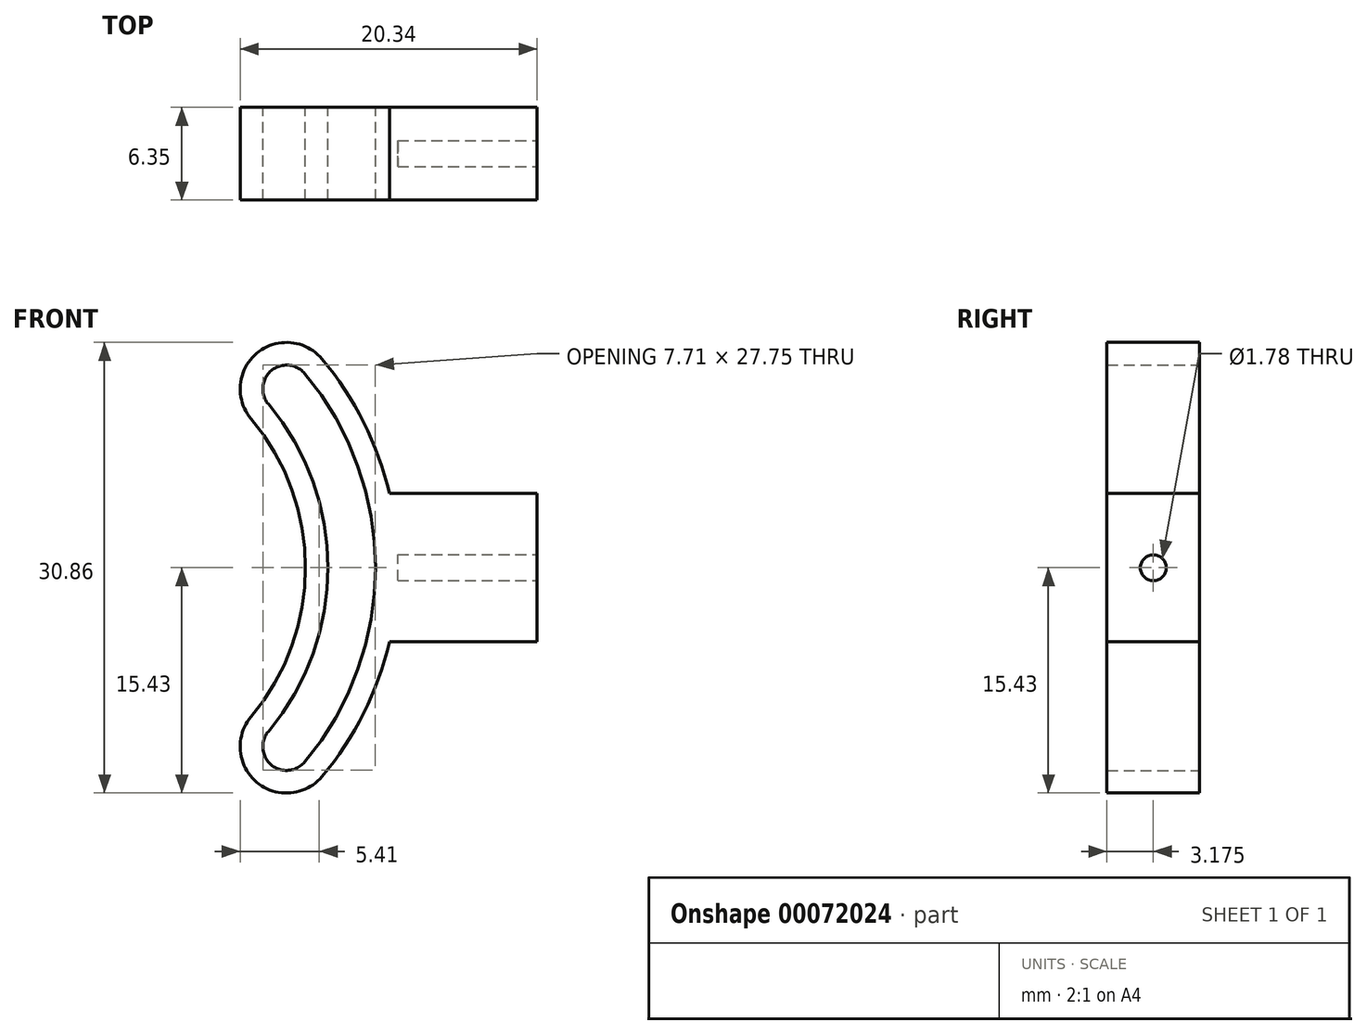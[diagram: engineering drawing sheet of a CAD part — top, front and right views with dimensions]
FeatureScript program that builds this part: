
annotation { "Feature Type Name" : "Feature", "Feature Type Description" : "" }
export const myFeature = defineFeature(function(context is Context, id is Id, definition is map)
    precondition{}
    {
        {
            var Q0;
            Q0=qCreatedBy(makeId("Front.planeOp"),FACE);
            var sketch = newSketch(context, id + "F0", { "sketchPlane" : qUnion([Q0])});
            skLineSegment(sketch, "E0.rect.bottom", {"start": v(5.08, 5.08) * mm, "end": v(-5.08, 5.08) * mm});
            skLineSegment(sketch, "E0.rect.top", {"start": v(5.08, -5.08) * mm, "end": v(-5.08, -5.08) * mm});
            skLineSegment(sketch, "E0.rect.left", {"start": v(5.08, 5.08) * mm, "end": v(5.08, -5.08) * mm});
            skLineSegment(sketch, "E0.rect.right", {"start": v(-5.08, 5.08) * mm, "end": v(-5.08, -5.08) * mm});
            skPoint(sketch, "E0.rect.middle", {"position": v(0, 0) * mm});
            skSolve(sketch);
        }
        {
            var Q0;
            Q0 = qSketchRegion(id + "F0", true);
            extrude(context, id + "F1", {"entities" : qUnion([Q0]), "depth" : 6.35 * mm});
        }
        {
            var Q0;
            Q0=makeQuery(id+"F1.opExtrude","SWEPT_FACE",FACE,{"disambiguationData":[OSD([sQuery(id+"F0.wireOp",EDGE,"E0.rect.left")])]});
            var sketch = newSketch(context, id + "F2", { "sketchPlane" : qUnion([Q0])});
            skCircle(sketch, "E1", {"center": v(-3.18, 0) * mm, "radius": 0.89 * mm});
            skPoint(sketch, "E1.centerSnap0", {"position": v(-6.35, 0) * mm});
            skSolve(sketch);
        }
        {
            var Q0;
            Q0 = qSketchRegion(id + "F2", true);
            extrude(context, id + "F3", {"entities" : qUnion([Q0]), "operationType" : NewBodyOperationType.REMOVE, "oppositeDirection" : true, "depth" : 25.4 * mm});
        }
        {
            var Q0;
            Q0=qCreatedBy(makeId("Front.planeOp"),FACE);
            var sketch = newSketch(context, id + "F4", { "sketchPlane" : qUnion([Q0])});
            skArc(sketch, "E2", {"start": v(-9.65, -14.3) * mm, "mid": v(-4.45, 0) * mm, "end": v(-9.65, 14.3) * mm});
            skArc(sketch, "E3", {"start": v(-9.65, 14.3) * mm, "mid": v(-14.13, 14.69) * mm, "end": v(-14.52, 10.21) * mm});
            skArc(sketch, "E4", {"start": v(-14.52, -10.21) * mm, "mid": v(-10.8, 0) * mm, "end": v(-14.52, 10.21) * mm});
            skArc(sketch, "E5", {"start": v(-14.52, -10.21) * mm, "mid": v(-14.13, -14.69) * mm, "end": v(-9.65, -14.3) * mm});
            skArc(sketch, "E6", {"start": v(-10.84, -13.3) * mm, "mid": v(-6, 0) * mm, "end": v(-10.84, 13.3) * mm});
            skArc(sketch, "E7", {"start": v(-10.84, 13.3) * mm, "mid": v(-13.13, 13.5) * mm, "end": v(-13.33, 11.2) * mm});
            skArc(sketch, "E8", {"start": v(-13.33, -11.2) * mm, "mid": v(-9.25, 0) * mm, "end": v(-13.33, 11.2) * mm});
            skArc(sketch, "E9", {"start": v(-13.33, -11.2) * mm, "mid": v(-13.13, -13.5) * mm, "end": v(-10.84, -13.3) * mm});
            skSolve(sketch);
        }
        {
            var Q0;
            Q0 = qSketchRegion(id + "F4", true);
            extrude(context, id + "F5", {"entities" : qUnion([Q0]), "operationType" : NewBodyOperationType.ADD, "depth" : 6.35 * mm});
        }
    });
